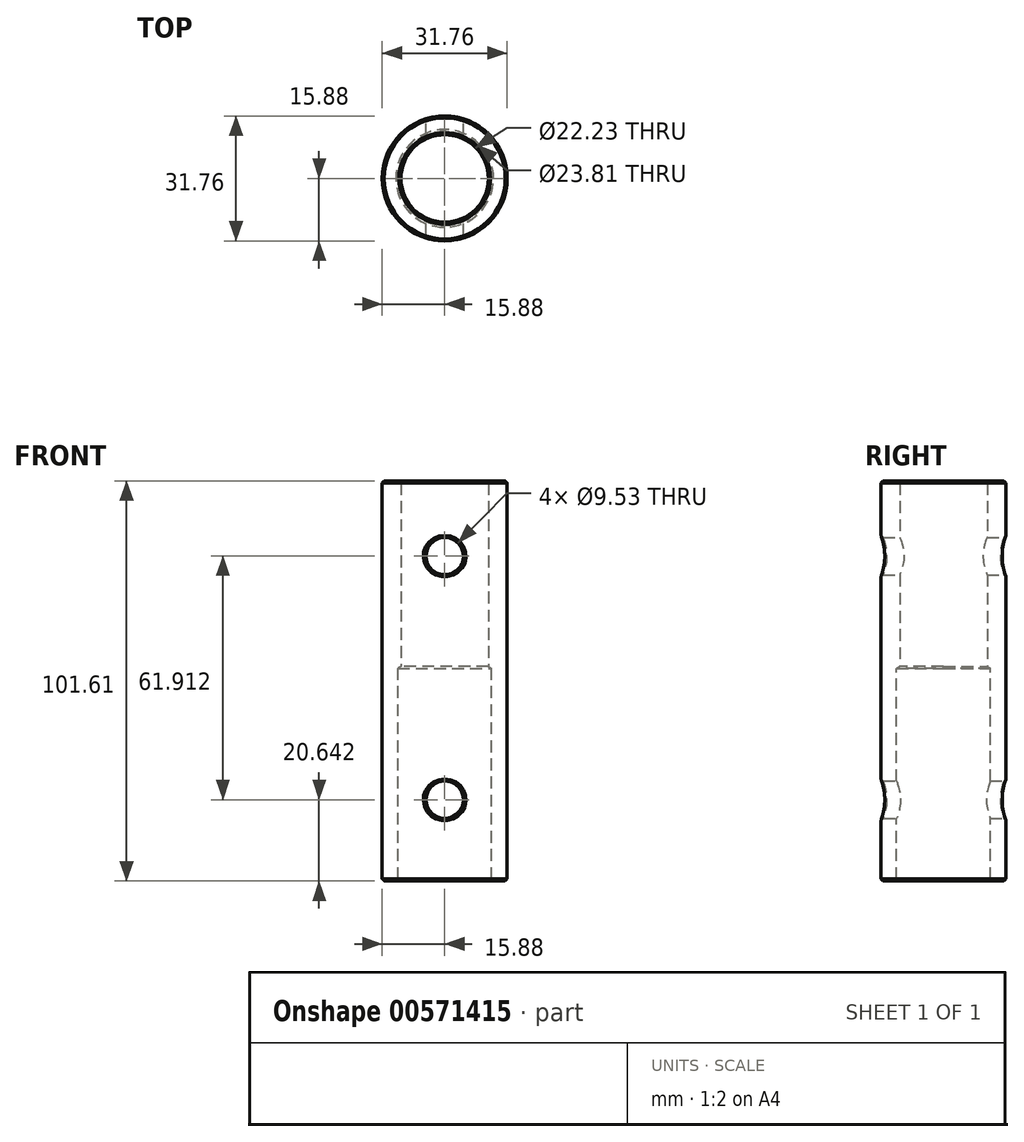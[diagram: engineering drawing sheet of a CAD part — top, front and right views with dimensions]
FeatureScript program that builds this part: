
annotation { "Feature Type Name" : "Feature", "Feature Type Description" : "" }
export const myFeature = defineFeature(function(context is Context, id is Id, definition is map)
    precondition{}
    {
        {
            var Q0;
            Q0=qCreatedBy(makeId("Top.planeOp"),FACE);
            var sketch = newSketch(context, id + "F0", { "sketchPlane" : qUnion([Q0])});
            skCircle(sketch, "E0", {"center": v(0, 0) * mm, "radius": 11.11 * mm});
            skCircle(sketch, "E1", {"center": v(0, 0) * mm, "radius": 15.88 * mm});
            skSolve(sketch);
        }
        {
            var Q0;
            Q0 = qSketchRegion(id + "F0", true);
            extrude(context, id + "F1", {"entities" : qUnion([Q0]), "depth" : 47.62 * mm, "offsetDistance" : 25.4 * mm});
        }
        {
            var Q0;
            Q0=makeQuery(id+"F1.opExtrude","CAP_FACE",FACE,{"disambiguationData":[OSD([sQuery(id+"F0.wireOp",EDGE,"E0"),sQuery(id+"F0.wireOp",EDGE,"E1")])],"isStart":true});
            var sketch = newSketch(context, id + "F2", { "sketchPlane" : qUnion([Q0])});
            skCircle(sketch, "E2", {"center": v(0, 0) * mm, "radius": 15.88 * mm});
            skCircle(sketch, "E3", {"center": v(0, 0) * mm, "radius": 11.9 * mm});
            skSolve(sketch);
        }
        {
            var Q0;
            Q0 = qSketchRegion(id + "F2", true);
            extrude(context, id + "F3", {"entities" : qUnion([Q0]), "operationType" : NewBodyOperationType.ADD, "depth" : 53.97 * mm, "offsetDistance" : 25.4 * mm});
        }
        {
            var Q0;
            Q0=qCreatedBy(makeId("Front.planeOp"),FACE);
            var sketch = newSketch(context, id + "F4", { "sketchPlane" : qUnion([Q0])});
            skCircle(sketch, "E4", {"center": v(0, 28.58) * mm, "radius": 4.76 * mm});
            skCircle(sketch, "E5", {"center": v(0, -33.34) * mm, "radius": 4.76 * mm});
            skSolve(sketch);
        }
        {
            var Q0;
            Q0 = qSketchRegion(id + "F4", true);
            extrude(context, id + "F5", {"entities" : qUnion([Q0]), "operationType" : NewBodyOperationType.REMOVE, "endBound" : BoundingType.SYMMETRIC, "depth" : 50.8 * mm, "offsetDistance" : 25.4 * mm});
        }
        {
            var Q0;
            Q0=makeQuery(id+"F3.opExtrude","CAP_EDGE",EDGE,{"disambiguationData":[OSD([sQuery(id+"F2.wireOp",EDGE,"E2")])],"isStart":false});
            var Q1;
            Q1=makeQuery(id+"F1.opExtrude","CAP_EDGE",EDGE,{"disambiguationData":[OSD([sQuery(id+"F0.wireOp",EDGE,"E1")])],"isStart":false});
            var Q2;
            Q2=makeQuery(id+"F3.opExtrude","CAP_EDGE",EDGE,{"disambiguationData":[OSD([sQuery(id+"F2.wireOp",EDGE,"E3")])],"isStart":false});
            var Q3;
            Q3=makeQuery(id+"F1.opExtrude","CAP_EDGE",EDGE,{"disambiguationData":[OSD([sQuery(id+"F0.wireOp",EDGE,"E0")])],"isStart":false});
            var Q4;
            Q4=makeQuery(id+"F5.boolean.opBoolean","INTERSECT",EDGE,{"disambiguationData":[OD(0.0)],"derivedFrom":[makeQuery(id+"F3.opExtrude","SWEPT_FACE",FACE,{"disambiguationData":[OSD([sQuery(id+"F2.wireOp",EDGE,"E2")])]}),makeQuery(id+"F5.opExtrude","SWEPT_FACE",FACE,{"disambiguationData":[OSD([sQuery(id+"F4.wireOp",EDGE,"E5")])]})]});
            var Q5;
            Q5=makeQuery(id+"F5.boolean.opBoolean","INTERSECT",EDGE,{"disambiguationData":[OD(0.0)],"derivedFrom":[makeQuery(id+"F1.opExtrude","SWEPT_FACE",FACE,{"disambiguationData":[OSD([sQuery(id+"F0.wireOp",EDGE,"E1")])]}),makeQuery(id+"F5.opExtrude","SWEPT_FACE",FACE,{"disambiguationData":[OSD([sQuery(id+"F4.wireOp",EDGE,"E4")])]})]});
            var Q6;
            Q6=makeQuery(id+"F5.boolean.opBoolean","INTERSECT",EDGE,{"disambiguationData":[OD(1.0)],"derivedFrom":[makeQuery(id+"F1.opExtrude","SWEPT_FACE",FACE,{"disambiguationData":[OSD([sQuery(id+"F0.wireOp",EDGE,"E1")])]}),makeQuery(id+"F5.opExtrude","SWEPT_FACE",FACE,{"disambiguationData":[OSD([sQuery(id+"F4.wireOp",EDGE,"E4")])]})]});
            var Q7;
            Q7=makeQuery(id+"F5.boolean.opBoolean","INTERSECT",EDGE,{"disambiguationData":[OD(1.0)],"derivedFrom":[makeQuery(id+"F3.opExtrude","SWEPT_FACE",FACE,{"disambiguationData":[OSD([sQuery(id+"F2.wireOp",EDGE,"E2")])]}),makeQuery(id+"F5.opExtrude","SWEPT_FACE",FACE,{"disambiguationData":[OSD([sQuery(id+"F4.wireOp",EDGE,"E5")])]})]});
            chamfer(context, id + "F6", {"entities" : qUnion([Q0, Q1, Q2, Q3, Q4, Q5, Q6, Q7]), "width" : 0.5 * mm, "tangentPropagation" : true});
        }
        {
            var Q0;
            Q0=makeQuery(id+"F1.opExtrude","CAP_EDGE",EDGE,{"disambiguationData":[OSD([sQuery(id+"F0.wireOp",EDGE,"E0")])],"isStart":true});
            chamfer(context, id + "F7", {"entities" : qUnion([Q0]), "chamferType" : ChamferType.OFFSET_ANGLE, "width" : 0.5 * mm, "oppositeDirection" : true, "angle" : 59 * degree, "tangentPropagation" : true});
        }
    });
